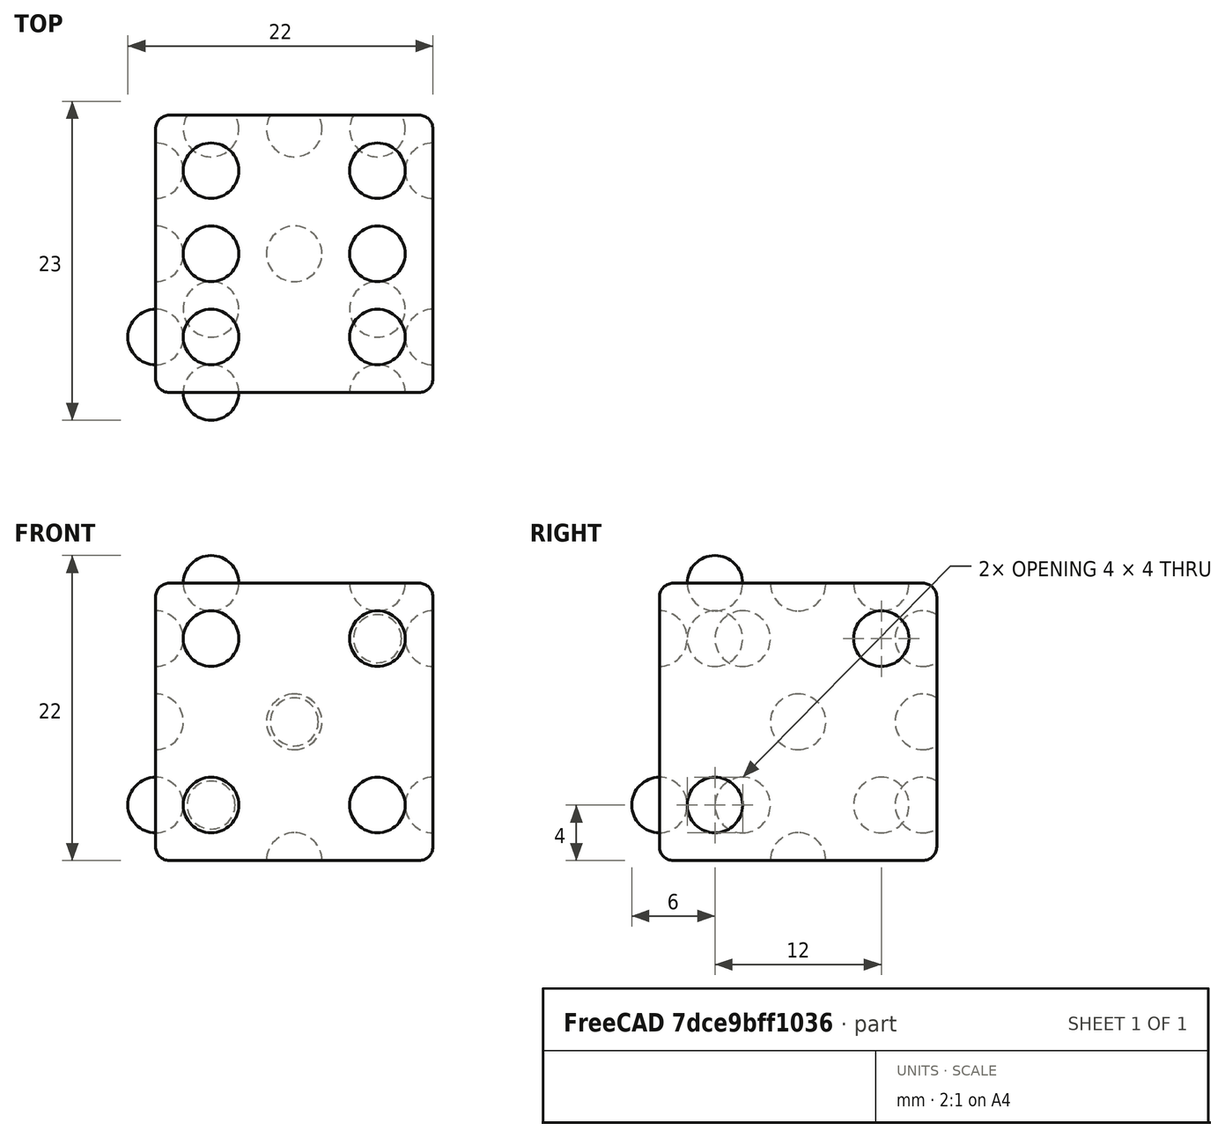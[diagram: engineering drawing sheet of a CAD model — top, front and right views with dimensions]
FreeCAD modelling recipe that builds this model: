
FCSTD DOCUMENT  (FreeCAD 0.21R33694 (Git))
Label: OJT1_T13R02_dau
License: All rights reserved
LicenseURL: https://en.wikipedia.org/wiki/All_rights_reserved
objects: Part::Sphere×10, Part::Cut×10, Part::Fillet×5, Part::FeaturePython×3, Part::Box×1
note: 26 computed .brp shape members not serialized (recipe doc carries the construction recipe); baked Part::Feature solids carry a one-line shape summary decoded from their .brp

FEATURE [Part::Box] Box  label="Cub"
  AttacherType = Attacher::AttachEngine3D
  Height = 20
  Length = 20
  Width = 20
FEATURE [Part::Fillet] Fillet
  Base = -> Box
  Edges = 1 edges r=1: [Edge10]
FEATURE [Part::Fillet] Fillet001
  Base = -> Fillet
  Edges = 1 edges r=1: [Edge4]
FEATURE [Part::Fillet] Fillet002
  Base = -> Fillet001
  Edges = 1 edges r=1: [Edge11]
FEATURE [Part::Fillet] Fillet003
  Base = -> Fillet002
  Edges = 1 edges r=1: [Edge7]
FEATURE [Part::Fillet] Fillet004
  Base = -> Fillet003
  Edges = 1 edges r=1: [Edge3]
FEATURE [Part::Sphere] Sphere  label="Esfera"
  Angle1 = -90
  Angle2 = 90
  Angle3 = 360
  AttacherType = Attacher::AttachEngine3D
  Placement = pos=(4,4,20) rot=(0,0,1;0rad)
  Radius = 2
FEATURE [Part::FeaturePython] Array  # Draft array (typed FeaturePython)
  AlwaysSyncPlacement = false
  Angle = 360
  ArrayType = 0
  Axis = (0,0,1)
  Base = -> Sphere
  Center = (0,0,0)
  Count = 6
  ExpandArray = false
  Fuse = false
  IntervalAxis = (0,0,0)
  IntervalX = (12,0,0)
  IntervalY = (0,6,0)
  IntervalZ = (0,0,100)
  NumberCircles = 3
  NumberPolar = 5
  NumberX = 2
  NumberY = 3
  NumberZ = 1
  PlacementList = 6 placements: [(4,4,20),(4,10,20),(4,16,20),(16,4,20),(16,10,20),(16,16,20)]
  RadialDistance = 50
  ScaleList = (6) [(1,1,1),(1,1,1),(1,1,1),(1,1,1),(1,1,1),(1,1,1)]
  Symmetry = 1
  TangentialDistance = 25
FEATURE [Part::Cut] Cut  label="Cara_6"
  Base = -> Fillet004
  Tool = -> Array
FEATURE [Part::Sphere] Sphere001  label="Esfera001"
  Angle1 = -90
  Angle2 = 90
  Angle3 = 360
  AttacherType = Attacher::AttachEngine3D
  Placement = pos=(4,0,4) rot=(0,0,1;0rad)
  Radius = 2
FEATURE [Part::FeaturePython] Array001  # Draft array (typed FeaturePython)
  AlwaysSyncPlacement = false
  Angle = 360
  ArrayType = 0
  Axis = (0,0,1)
  Base = -> Sphere001
  Center = (0,0,0)
  Count = 8
  ExpandArray = false
  Fuse = false
  IntervalAxis = (0,0,0)
  IntervalX = (12,0,0)
  IntervalY = (0,6,0)
  IntervalZ = (0,0,12)
  NumberCircles = 3
  NumberPolar = 5
  NumberX = 2
  NumberY = 2
  NumberZ = 2
  PlacementList = 8 placements: [(4,0,4),(4,0,16),(4,6,4),(4,6,16),(16,0,4),(16,0,16),(16,6,4),(16,6,16)]
  RadialDistance = 50
  ScaleList = (8) [(1,1,1),(1,1,1),(1,1,1),(1,1,1),(1,1,1),(1,1,1),(1,1,1),(1,1,1)]
  Symmetry = 1
  TangentialDistance = 25
FEATURE [Part::Cut] Cut001
  Base = -> Cut
  Tool = -> Array001
FEATURE [Part::Sphere] Sphere002  label="Esfera002"
  Angle1 = -90
  Angle2 = 90
  Angle3 = 360
  AttacherType = Attacher::AttachEngine3D
  Placement = pos=(0,10,10) rot=(0,0,1;0rad)
  Radius = 2
FEATURE [Part::Sphere] Sphere003  label="Esfera003"
  Angle1 = -90
  Angle2 = 90
  Angle3 = 360
  AttacherType = Attacher::AttachEngine3D
  Placement = pos=(0,4,4) rot=(0,0,1;0rad)
  Radius = 2
FEATURE [Part::FeaturePython] Array002  # Draft array (typed FeaturePython)
  AlwaysSyncPlacement = false
  Angle = 360
  ArrayType = 0
  Axis = (0,0,1)
  Base = -> Sphere003
  Center = (0,0,0)
  Count = 4
  ExpandArray = false
  Fuse = false
  IntervalAxis = (0,0,0)
  IntervalX = (6,0,0)
  IntervalY = (0,12,0)
  IntervalZ = (0,0,12)
  NumberCircles = 3
  NumberPolar = 5
  NumberX = 1
  NumberY = 2
  NumberZ = 2
  PlacementList = 4 placements: [(0,4,4),(0,4,16),(0,16,4),(0,16,16)]
  RadialDistance = 50
  ScaleList = (4) [(1,1,1),(1,1,1),(1,1,1),(1,1,1)]
  Symmetry = 1
  TangentialDistance = 25
FEATURE [Part::Cut] Cut002
  Base = -> Cut001
  Tool = -> Array002
FEATURE [Part::Cut] Cut003
  Base = -> Cut002
  Tool = -> Sphere002
FEATURE [Part::Sphere] Sphere004  label="Esfera004"
  Angle1 = -90
  Angle2 = 90
  Angle3 = 360
  AttacherType = Attacher::AttachEngine3D
  Placement = pos=(4,19,4) rot=(0,0,1;0rad)
  Radius = 2
FEATURE [Part::Cut] Cut004
  Base = -> Cut003
  Tool = -> Sphere004
FEATURE [Part::Sphere] Sphere005  label="Esfera005"
  Angle1 = -90
  Angle2 = 90
  Angle3 = 360
  AttacherType = Attacher::AttachEngine3D
  Placement = pos=(10,19,10) rot=(0,0,1;0rad)
  Radius = 2
FEATURE [Part::Cut] Cut005
  Base = -> Cut004
  Tool = -> Sphere005
FEATURE [Part::Sphere] Sphere006  label="Esfera006"
  Angle1 = -90
  Angle2 = 90
  Angle3 = 360
  AttacherType = Attacher::AttachEngine3D
  Placement = pos=(16,19,16) rot=(0,0,1;0rad)
  Radius = 2
FEATURE [Part::Cut] Cut006
  Base = -> Cut005
  Tool = -> Sphere006
FEATURE [Part::Sphere] Sphere007  label="Esfera007"
  Angle1 = -90
  Angle2 = 90
  Angle3 = 360
  AttacherType = Attacher::AttachEngine3D
  Placement = pos=(10,10,0) rot=(0,0,1;0rad)
  Radius = 2
FEATURE [Part::Cut] Cut007
  Base = -> Cut006
  Tool = -> Sphere007
FEATURE [Part::Sphere] Sphere008  label="Esfera008"
  Angle1 = -90
  Angle2 = 90
  Angle3 = 360
  AttacherType = Attacher::AttachEngine3D
  Placement = pos=(20,4,4) rot=(0,0,1;0rad)
  Radius = 2
FEATURE [Part::Cut] Cut008
  Base = -> Cut007
  Tool = -> Sphere008
FEATURE [Part::Sphere] Sphere009  label="Esfera009"
  Angle1 = -90
  Angle2 = 90
  Angle3 = 360
  AttacherType = Attacher::AttachEngine3D
  Placement = pos=(20,16,16) rot=(0,0,1;0rad)
  Radius = 2
FEATURE [Part::Cut] Cut009
  Base = -> Cut008
  Tool = -> Sphere009
